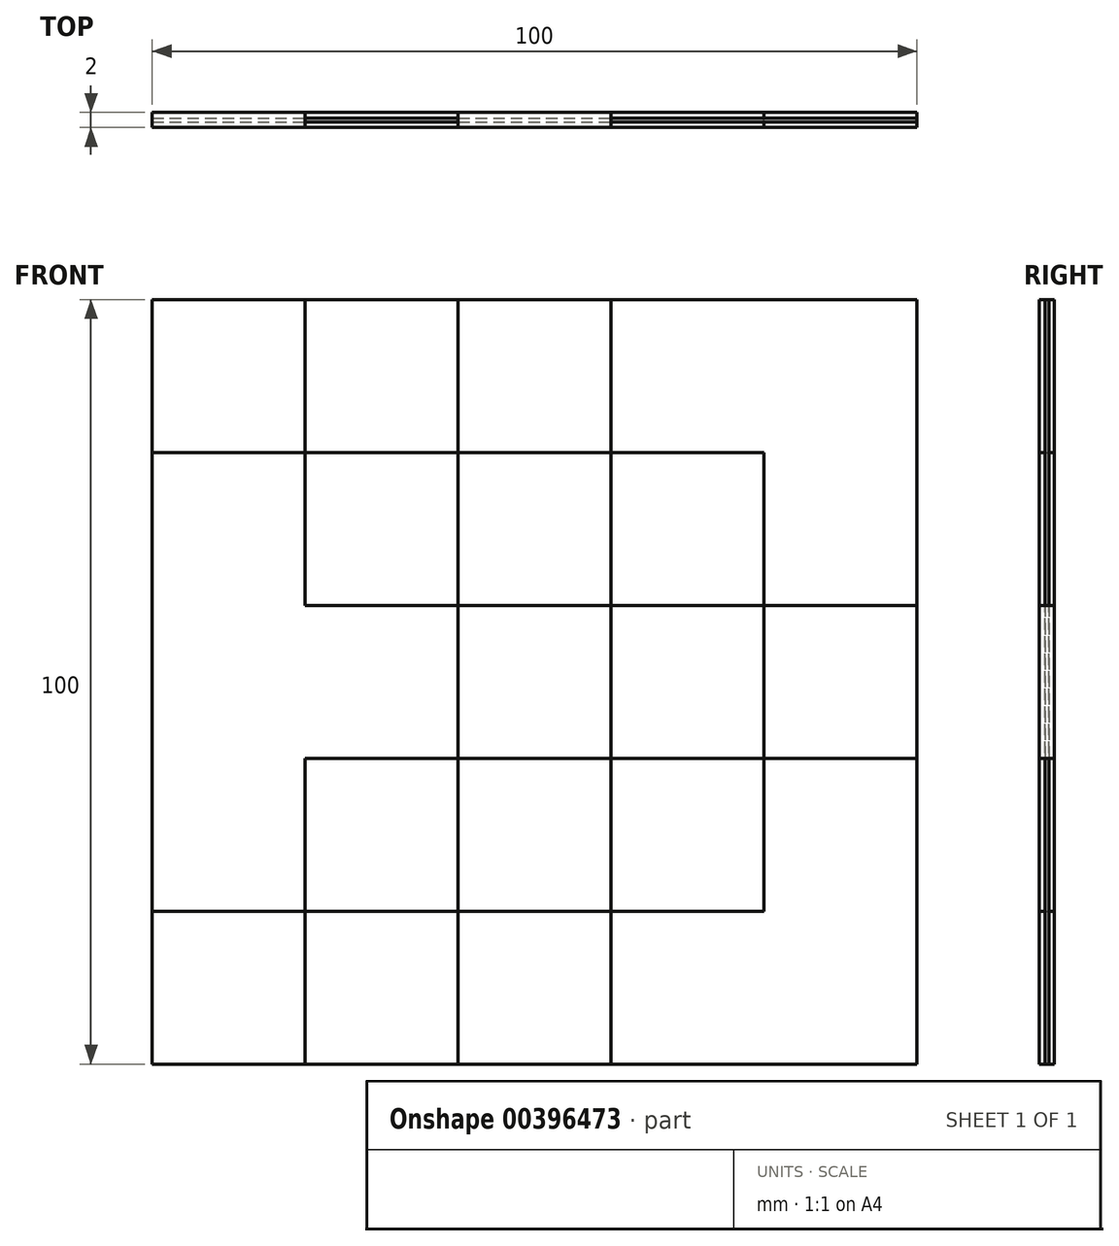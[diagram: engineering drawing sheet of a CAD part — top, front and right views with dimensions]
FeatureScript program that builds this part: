
annotation { "Feature Type Name" : "Feature", "Feature Type Description" : "" }
export const myFeature = defineFeature(function(context is Context, id is Id, definition is map)
    precondition{}
    {
        {
            var Q0;
            Q0=qCreatedBy(makeId("Front.planeOp"),FACE);
            var sketch = newSketch(context, id + "F0", { "sketchPlane" : qUnion([Q0])});
            skLineSegment(sketch, "E0.bottom", {"start": v(50, -50) * mm, "end": v(-50, -50) * mm});
            skLineSegment(sketch, "E0.top", {"start": v(50, 50) * mm, "end": v(-50, 50) * mm});
            skLineSegment(sketch, "E0.left", {"start": v(50, -50) * mm, "end": v(50, 50) * mm});
            skLineSegment(sketch, "E0.right", {"start": v(-50, -50) * mm, "end": v(-50, 50) * mm});
            skPoint(sketch, "E0.middle", {"position": v(0, 0) * mm});
            skLineSegment(sketch, "E1", {"start": v(-50, 30) * mm, "end": v(50, 30) * mm});
            skLineSegment(sketch, "E2", {"start": v(-50, 10) * mm, "end": v(50, 10) * mm});
            skLineSegment(sketch, "E3", {"start": v(-50, -10) * mm, "end": v(50, -10) * mm});
            skLineSegment(sketch, "E4", {"start": v(-50, -30) * mm, "end": v(50, -30) * mm});
            skLineSegment(sketch, "E5", {"start": v(-30, 50) * mm, "end": v(-30, -50) * mm});
            skLineSegment(sketch, "E6", {"start": v(-10, 50) * mm, "end": v(-10, -50) * mm});
            skLineSegment(sketch, "E7", {"start": v(10, 50) * mm, "end": v(10, -50) * mm});
            skLineSegment(sketch, "E8", {"start": v(30, 50) * mm, "end": v(30, -50) * mm});
            skSolve(sketch);
        }
        {
            var Q0;
            {var subQ0=sQuery(id+"F0.wireOp",EDGE,"E0.right");var subQ1=sQuery(id+"F0.wireOp",EDGE,"E0.top");var subQ2=makeQuery(id+"F0.imprint","INTERSECT",VERTEX,{"derivedFrom":[subQ1,subQ0]});Q0=makeQuery(id+"F0.imprint","IMPRINT",FACE,{"disambiguationData":[TD([[makeQuery(id+"F0.imprint","IMPRINT",EDGE,{"disambiguationData":[TD([[subQ2,1.0]])],"derivedFrom":subQ1}),1.0]])]});}
            var Q1;
            {var subQ0=sQuery(id+"F0.wireOp",EDGE,"E5");var subQ1=sQuery(id+"F0.wireOp",EDGE,"E1");var subQ2=makeQuery(id+"F0.imprint","INTERSECT",VERTEX,{"derivedFrom":[subQ1,subQ0]});Q1=makeQuery(id+"F0.imprint","IMPRINT",FACE,{"disambiguationData":[TD([[makeQuery(id+"F0.imprint","IMPRINT",EDGE,{"disambiguationData":[TD([[subQ2,-1.0]])],"derivedFrom":subQ1}),-1.0]])]});}
            var Q2;
            {var subQ0=sQuery(id+"F0.wireOp",EDGE,"E6");var subQ1=sQuery(id+"F0.wireOp",EDGE,"E2");var subQ2=makeQuery(id+"F0.imprint","INTERSECT",VERTEX,{"derivedFrom":[subQ1,subQ0]});Q2=makeQuery(id+"F0.imprint","IMPRINT",FACE,{"disambiguationData":[TD([[makeQuery(id+"F0.imprint","IMPRINT",EDGE,{"disambiguationData":[TD([[subQ2,-1.0]])],"derivedFrom":subQ1}),-1.0]])]});}
            var Q3;
            {var subQ0=sQuery(id+"F0.wireOp",EDGE,"E5");var subQ1=sQuery(id+"F0.wireOp",EDGE,"E3");var subQ2=makeQuery(id+"F0.imprint","INTERSECT",VERTEX,{"derivedFrom":[subQ1,subQ0]});Q3=makeQuery(id+"F0.imprint","IMPRINT",FACE,{"disambiguationData":[TD([[makeQuery(id+"F0.imprint","IMPRINT",EDGE,{"disambiguationData":[TD([[subQ2,-1.0]])],"derivedFrom":subQ1}),-1.0]])]});}
            var Q4;
            {var subQ0=sQuery(id+"F0.wireOp",EDGE,"E0.right");var subQ1=sQuery(id+"F0.wireOp",EDGE,"E0.bottom");var subQ2=makeQuery(id+"F0.imprint","INTERSECT",VERTEX,{"derivedFrom":[subQ1,subQ0]});Q4=makeQuery(id+"F0.imprint","IMPRINT",FACE,{"disambiguationData":[TD([[makeQuery(id+"F0.imprint","IMPRINT",EDGE,{"disambiguationData":[TD([[subQ2,1.0]])],"derivedFrom":subQ1}),-1.0]])]});}
            var Q5;
            {var subQ0=sQuery(id+"F0.wireOp",EDGE,"E6");var subQ1=sQuery(id+"F0.wireOp",EDGE,"E0.top");var subQ2=makeQuery(id+"F0.imprint","INTERSECT",VERTEX,{"derivedFrom":[subQ1,subQ0]});Q5=makeQuery(id+"F0.imprint","IMPRINT",FACE,{"disambiguationData":[TD([[makeQuery(id+"F0.imprint","IMPRINT",EDGE,{"disambiguationData":[TD([[subQ2,1.0]])],"derivedFrom":subQ1}),1.0]])]});}
            var Q6;
            {var subQ0=sQuery(id+"F0.wireOp",EDGE,"E7");var subQ1=sQuery(id+"F0.wireOp",EDGE,"E1");var subQ2=makeQuery(id+"F0.imprint","INTERSECT",VERTEX,{"derivedFrom":[subQ1,subQ0]});Q6=makeQuery(id+"F0.imprint","IMPRINT",FACE,{"disambiguationData":[TD([[makeQuery(id+"F0.imprint","IMPRINT",EDGE,{"disambiguationData":[TD([[subQ2,-1.0]])],"derivedFrom":subQ1}),-1.0]])]});}
            var Q7;
            {var subQ0=sQuery(id+"F0.wireOp",EDGE,"E2");var subQ1=sQuery(id+"F0.wireOp",EDGE,"E0.left");var subQ2=makeQuery(id+"F0.imprint","INTERSECT",VERTEX,{"derivedFrom":[subQ1,subQ0]});Q7=makeQuery(id+"F0.imprint","IMPRINT",FACE,{"disambiguationData":[TD([[makeQuery(id+"F0.imprint","IMPRINT",EDGE,{"disambiguationData":[TD([[subQ2,1.0]])],"derivedFrom":subQ1}),1.0]])]});}
            var Q8;
            {var subQ0=sQuery(id+"F0.wireOp",EDGE,"E7");var subQ1=sQuery(id+"F0.wireOp",EDGE,"E3");var subQ2=makeQuery(id+"F0.imprint","INTERSECT",VERTEX,{"derivedFrom":[subQ1,subQ0]});Q8=makeQuery(id+"F0.imprint","IMPRINT",FACE,{"disambiguationData":[TD([[makeQuery(id+"F0.imprint","IMPRINT",EDGE,{"disambiguationData":[TD([[subQ2,-1.0]])],"derivedFrom":subQ1}),-1.0]])]});}
            var Q9;
            {var subQ0=sQuery(id+"F0.wireOp",EDGE,"E6");var subQ1=sQuery(id+"F0.wireOp",EDGE,"E0.bottom");var subQ2=makeQuery(id+"F0.imprint","INTERSECT",VERTEX,{"derivedFrom":[subQ1,subQ0]});Q9=makeQuery(id+"F0.imprint","IMPRINT",FACE,{"disambiguationData":[TD([[makeQuery(id+"F0.imprint","IMPRINT",EDGE,{"disambiguationData":[TD([[subQ2,1.0]])],"derivedFrom":subQ1}),-1.0]])]});}
            extrude(context, id + "F1", {"entities" : qUnion([Q0, Q1, Q2, Q3, Q4, Q5, Q6, Q7, Q8, Q9]), "endBound" : BoundingType.SYMMETRIC, "depth" : 2 * mm});
        }
        {
            var Q0;
            {var subQ0=sQuery(id+"F0.wireOp",EDGE,"E1");var subQ1=sQuery(id+"F0.wireOp",EDGE,"E0.right");var subQ2=makeQuery(id+"F0.imprint","INTERSECT",VERTEX,{"derivedFrom":[subQ1,subQ0]});Q0=makeQuery(id+"F0.imprint","IMPRINT",FACE,{"disambiguationData":[TD([[makeQuery(id+"F0.imprint","IMPRINT",EDGE,{"disambiguationData":[TD([[subQ2,1.0]])],"derivedFrom":subQ1}),-1.0]])]});}
            var Q1;
            {var subQ0=sQuery(id+"F0.wireOp",EDGE,"E2");var subQ1=sQuery(id+"F0.wireOp",EDGE,"E0.right");var subQ2=makeQuery(id+"F0.imprint","INTERSECT",VERTEX,{"derivedFrom":[subQ1,subQ0]});Q1=makeQuery(id+"F0.imprint","IMPRINT",FACE,{"disambiguationData":[TD([[makeQuery(id+"F0.imprint","IMPRINT",EDGE,{"disambiguationData":[TD([[subQ2,1.0]])],"derivedFrom":subQ1}),-1.0]])]});}
            var Q2;
            {var subQ0=sQuery(id+"F0.wireOp",EDGE,"E3");var subQ1=sQuery(id+"F0.wireOp",EDGE,"E0.right");var subQ2=makeQuery(id+"F0.imprint","INTERSECT",VERTEX,{"derivedFrom":[subQ1,subQ0]});Q2=makeQuery(id+"F0.imprint","IMPRINT",FACE,{"disambiguationData":[TD([[makeQuery(id+"F0.imprint","IMPRINT",EDGE,{"disambiguationData":[TD([[subQ2,1.0]])],"derivedFrom":subQ1}),-1.0]])]});}
            var Q3;
            {var subQ0=sQuery(id+"F0.wireOp",EDGE,"E5");var subQ1=sQuery(id+"F0.wireOp",EDGE,"E2");var subQ2=makeQuery(id+"F0.imprint","INTERSECT",VERTEX,{"derivedFrom":[subQ1,subQ0]});Q3=makeQuery(id+"F0.imprint","IMPRINT",FACE,{"disambiguationData":[TD([[makeQuery(id+"F0.imprint","IMPRINT",EDGE,{"disambiguationData":[TD([[subQ2,-1.0]])],"derivedFrom":subQ1}),-1.0]])]});}
            var Q4;
            {var subQ0=sQuery(id+"F0.wireOp",EDGE,"E5");var subQ1=sQuery(id+"F0.wireOp",EDGE,"E0.top");var subQ2=makeQuery(id+"F0.imprint","INTERSECT",VERTEX,{"derivedFrom":[subQ1,subQ0]});Q4=makeQuery(id+"F0.imprint","IMPRINT",FACE,{"disambiguationData":[TD([[makeQuery(id+"F0.imprint","IMPRINT",EDGE,{"disambiguationData":[TD([[subQ2,1.0]])],"derivedFrom":subQ1}),1.0]])]});}
            var Q5;
            {var subQ0=sQuery(id+"F0.wireOp",EDGE,"E6");var subQ1=sQuery(id+"F0.wireOp",EDGE,"E1");var subQ2=makeQuery(id+"F0.imprint","INTERSECT",VERTEX,{"derivedFrom":[subQ1,subQ0]});Q5=makeQuery(id+"F0.imprint","IMPRINT",FACE,{"disambiguationData":[TD([[makeQuery(id+"F0.imprint","IMPRINT",EDGE,{"disambiguationData":[TD([[subQ2,-1.0]])],"derivedFrom":subQ1}),-1.0]])]});}
            var Q6;
            {var subQ0=sQuery(id+"F0.wireOp",EDGE,"E7");var subQ1=sQuery(id+"F0.wireOp",EDGE,"E2");var subQ2=makeQuery(id+"F0.imprint","INTERSECT",VERTEX,{"derivedFrom":[subQ1,subQ0]});Q6=makeQuery(id+"F0.imprint","IMPRINT",FACE,{"disambiguationData":[TD([[makeQuery(id+"F0.imprint","IMPRINT",EDGE,{"disambiguationData":[TD([[subQ2,-1.0]])],"derivedFrom":subQ1}),-1.0]])]});}
            var Q7;
            {var subQ0=sQuery(id+"F0.wireOp",EDGE,"E6");var subQ1=sQuery(id+"F0.wireOp",EDGE,"E3");var subQ2=makeQuery(id+"F0.imprint","INTERSECT",VERTEX,{"derivedFrom":[subQ1,subQ0]});Q7=makeQuery(id+"F0.imprint","IMPRINT",FACE,{"disambiguationData":[TD([[makeQuery(id+"F0.imprint","IMPRINT",EDGE,{"disambiguationData":[TD([[subQ2,-1.0]])],"derivedFrom":subQ1}),-1.0]])]});}
            var Q8;
            {var subQ0=sQuery(id+"F0.wireOp",EDGE,"E5");var subQ1=sQuery(id+"F0.wireOp",EDGE,"E0.bottom");var subQ2=makeQuery(id+"F0.imprint","INTERSECT",VERTEX,{"derivedFrom":[subQ1,subQ0]});Q8=makeQuery(id+"F0.imprint","IMPRINT",FACE,{"disambiguationData":[TD([[makeQuery(id+"F0.imprint","IMPRINT",EDGE,{"disambiguationData":[TD([[subQ2,1.0]])],"derivedFrom":subQ1}),-1.0]])]});}
            var Q9;
            {var subQ0=sQuery(id+"F0.wireOp",EDGE,"E7");var subQ1=sQuery(id+"F0.wireOp",EDGE,"E0.bottom");var subQ2=makeQuery(id+"F0.imprint","INTERSECT",VERTEX,{"derivedFrom":[subQ1,subQ0]});Q9=makeQuery(id+"F0.imprint","IMPRINT",FACE,{"disambiguationData":[TD([[makeQuery(id+"F0.imprint","IMPRINT",EDGE,{"disambiguationData":[TD([[subQ2,1.0]])],"derivedFrom":subQ1}),-1.0]])]});}
            var Q10;
            {var subQ0=sQuery(id+"F0.wireOp",EDGE,"E0.left");var subQ1=sQuery(id+"F0.wireOp",EDGE,"E0.bottom");var subQ2=makeQuery(id+"F0.imprint","INTERSECT",VERTEX,{"derivedFrom":[subQ1,subQ0]});Q10=makeQuery(id+"F0.imprint","IMPRINT",FACE,{"disambiguationData":[TD([[makeQuery(id+"F0.imprint","IMPRINT",EDGE,{"disambiguationData":[TD([[subQ2,-1.0]])],"derivedFrom":subQ1}),-1.0]])]});}
            var Q11;
            {var subQ0=sQuery(id+"F0.wireOp",EDGE,"E3");var subQ1=sQuery(id+"F0.wireOp",EDGE,"E0.left");var subQ2=makeQuery(id+"F0.imprint","INTERSECT",VERTEX,{"derivedFrom":[subQ1,subQ0]});Q11=makeQuery(id+"F0.imprint","IMPRINT",FACE,{"disambiguationData":[TD([[makeQuery(id+"F0.imprint","IMPRINT",EDGE,{"disambiguationData":[TD([[subQ2,1.0]])],"derivedFrom":subQ1}),1.0]])]});}
            var Q12;
            {var subQ0=sQuery(id+"F0.wireOp",EDGE,"E1");var subQ1=sQuery(id+"F0.wireOp",EDGE,"E0.left");var subQ2=makeQuery(id+"F0.imprint","INTERSECT",VERTEX,{"derivedFrom":[subQ1,subQ0]});Q12=makeQuery(id+"F0.imprint","IMPRINT",FACE,{"disambiguationData":[TD([[makeQuery(id+"F0.imprint","IMPRINT",EDGE,{"disambiguationData":[TD([[subQ2,1.0]])],"derivedFrom":subQ1}),1.0]])]});}
            var Q13;
            {var subQ0=sQuery(id+"F0.wireOp",EDGE,"E0.left");var subQ1=sQuery(id+"F0.wireOp",EDGE,"E0.top");var subQ2=makeQuery(id+"F0.imprint","INTERSECT",VERTEX,{"derivedFrom":[subQ1,subQ0]});Q13=makeQuery(id+"F0.imprint","IMPRINT",FACE,{"disambiguationData":[TD([[makeQuery(id+"F0.imprint","IMPRINT",EDGE,{"disambiguationData":[TD([[subQ2,-1.0]])],"derivedFrom":subQ1}),1.0]])]});}
            var Q14;
            {var subQ0=sQuery(id+"F0.wireOp",EDGE,"E7");var subQ1=sQuery(id+"F0.wireOp",EDGE,"E0.top");var subQ2=makeQuery(id+"F0.imprint","INTERSECT",VERTEX,{"derivedFrom":[subQ1,subQ0]});Q14=makeQuery(id+"F0.imprint","IMPRINT",FACE,{"disambiguationData":[TD([[makeQuery(id+"F0.imprint","IMPRINT",EDGE,{"disambiguationData":[TD([[subQ2,1.0]])],"derivedFrom":subQ1}),1.0]])]});}
            extrude(context, id + "F2", {"entities" : qUnion([Q0, Q1, Q2, Q3, Q4, Q5, Q6, Q7, Q8, Q9, Q10, Q11, Q12, Q13, Q14]), "endBound" : BoundingType.SYMMETRIC, "depth" : 0.5 * mm});
        }
    });
